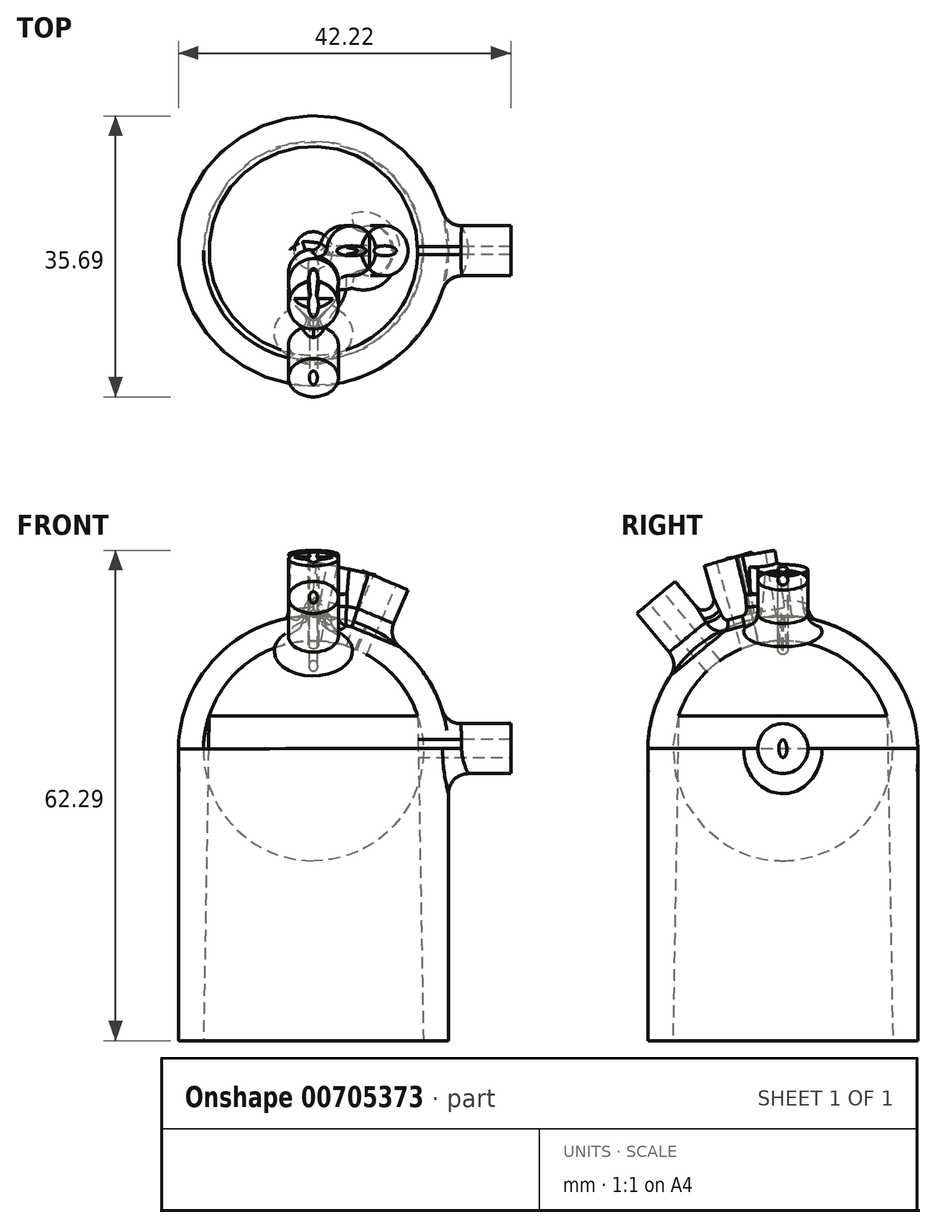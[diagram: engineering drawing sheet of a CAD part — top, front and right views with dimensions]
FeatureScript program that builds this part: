
annotation { "Feature Type Name" : "Feature", "Feature Type Description" : "" }
export const myFeature = defineFeature(function(context is Context, id is Id, definition is map)
    precondition{}
    {
        {
            var Q0;
            Q0=qCreatedBy(makeId("Front.planeOp"),FACE);
            var sketch = newSketch(context, id + "F0", { "sketchPlane" : qUnion([Q0])});
            skPoint(sketch, "E0.orphan", {"position": v(0, 0) * mm});
            skLineSegment(sketch, "E1.right", {"start": v(13.97, 0) * mm, "end": v(13.97, 37.07) * mm});
            skArc(sketch, "E2", {"start": v(13.97, 37.07) * mm, "mid": v(9.8, 46.8) * mm, "end": v(0, 50.8) * mm});
            skArc(sketch, "E3.0", {"start": v(17.14, 37.1) * mm, "mid": v(12.03, 49.05) * mm, "end": v(0, 53.98) * mm});
            skLineSegment(sketch, "E3.1", {"start": v(17.15, 0) * mm, "end": v(17.14, 37.1) * mm});
            skLineSegment(sketch, "E4", {"start": v(0, 53.98) * mm, "end": v(0, 50.8) * mm});
            skLineSegment(sketch, "E5", {"start": v(13.97, 0) * mm, "end": v(17.15, 0) * mm});
            skLineSegment(sketch, "E6", {"start": v(13.97, 0) * mm, "end": v(13.25, 41.26) * mm});
            skSolve(sketch);
        }
        {
            var Q0;
            Q0 = qSketchRegion(id + "F0", true);
            var Q1;
            Q1=sQuery(id+"F0.wireOp",EDGE,"E4");
            revolve(context, id + "F1", {"surfaceOperationType" : NewSurfaceOperationType.NEW, "entities" : qUnion([Q0]), "axis" : qUnion([Q1]), "revolveType" : RevolveType.FULL});
        }
        {
            var Q0;
            Q0=qCreatedBy(makeId("Front.planeOp"),FACE);
            var sketch = newSketch(context, id + "F2", { "sketchPlane" : qUnion([Q0])});
            skPoint(sketch, "E7", {"position": v(0, 37.1) * mm});
            skLineSegment(sketch, "E8", {"start": v(0, 37.1) * mm, "end": v(25.4, 37.1) * mm, "construction": true});
            skLineSegment(sketch, "E9", {"start": v(0, 37.1) * mm, "end": v(9.92, 60.47) * mm, "construction": true});
            skLineSegment(sketch, "E10", {"start": v(0, 37.1) * mm, "end": v(5.28, 61.94) * mm, "construction": true});
            skArc(sketch, "E11.0", {"start": v(6.6, 52.65) * mm, "mid": v(3.37, 53.64) * mm, "end": v(0, 53.98) * mm, "construction": true});
            skPoint(sketch, "E12.orphan", {"position": v(17.14, 37.1) * mm});
            skPoint(sketch, "E13", {"position": v(6.6, 52.65) * mm});
            skPoint(sketch, "E14", {"position": v(3.51, 53.61) * mm});
            skSolve(sketch);
        }
        {
            var Q0;
            Q0=sQuery(id+"F2.wireOp",VERTEX,"E13");
            var Q1;
            Q1=sQuery(id+"F2.wireOp",EDGE,"E9");
            cPlane(context, id + "F3", {"entities" : qUnion([Q0, Q1]), "cplaneType" : CPlaneType.LINE_POINT, "offset" : 25.4 * mm, "width" : 152.4 * mm, "height" : 152.4 * mm});
        }
        {
            var Q0;
            Q0=sQuery(id+"F2.wireOp",VERTEX,"E12.orphan");
            var Q1;
            Q1=sQuery(id+"F2.wireOp",EDGE,"E8");
            cPlane(context, id + "F4", {"entities" : qUnion([Q0, Q1]), "cplaneType" : CPlaneType.LINE_POINT, "offset" : 25.4 * mm, "width" : 152.4 * mm, "height" : 152.4 * mm});
        }
        {
            var Q0;
            Q0=sQuery(id+"F2.wireOp",VERTEX,"E14");
            var Q1;
            Q1=sQuery(id+"F2.wireOp",EDGE,"E10");
            cPlane(context, id + "F5", {"entities" : qUnion([Q0, Q1]), "cplaneType" : CPlaneType.LINE_POINT, "offset" : 25.4 * mm, "width" : 152.4 * mm, "height" : 152.4 * mm});
        }
        {
            var Q0;
            Q0=qCreatedBy(id+"F4.planeOp",FACE);
            var sketch = newSketch(context, id + "F6", { "sketchPlane" : qUnion([Q0])});
            skPoint(sketch, "E15.0", {"position": v(0, 37.1) * mm});
            skCircle(sketch, "E16", {"center": v(0, 37.1) * mm, "radius": 3.18 * mm});
            skSolve(sketch);
        }
        {
            var Q0;
            Q0=makeQuery(id+"F6.imprint","IMPRINT",FACE,{"disambiguationData":[TD([[makeQuery(id+"F6.imprint","IMPRINT",EDGE,{"derivedFrom":sQuery(id+"F6.wireOp",EDGE,"E16")}),1.0]])]});
            extrude(context, id + "F7", {"entities" : qUnion([Q0]), "operationType" : NewBodyOperationType.ADD, "endBound" : BoundingType.SYMMETRIC, "oppositeDirection" : true, "depth" : 3.17 * mm, "offsetDistance" : 25.4 * mm});
        }
        {
            var Q0;
            Q0=makeQuery(id+"F7.opExtrude","CAP_FACE",FACE,{"disambiguationData":[OSD([sQuery(id+"F6.wireOp",EDGE,"E16")])],"isStart":true});
            extrude(context, id + "F8", {"entities" : qUnion([Q0]), "operationType" : NewBodyOperationType.ADD, "depth" : 6.35 * mm, "offsetDistance" : 25.4 * mm});
        }
        {
            var Q0;
            Q0=makeQuery(id+"F8.opExtrude","CAP_FACE",FACE,{"disambiguationData":[OSD([sQuery(id+"F6.wireOp",EDGE,"E16")])],"isStart":false});
            var sketch = newSketch(context, id + "F9", { "sketchPlane" : qUnion([Q0])});
            skEllipse(sketch, "E17", {"center": v(0, 37.1) * mm, "majorRadius": 1.14 * mm, "minorRadius": 0.5 * mm, "majorAxis": v(0, -1)});
            skSolve(sketch);
        }
        {
            var Q0;
            Q0=makeQuery(id+"F9.imprint","IMPRINT",FACE,{"disambiguationData":[TD([[makeQuery(id+"F9.imprint","IMPRINT",EDGE,{"derivedFrom":sQuery(id+"F9.wireOp",EDGE,"E17")}),1.0]])]});
            var Q1;
            Q1=makeQuery(id+"F1.opRevolve","SWEPT_FACE",FACE,{"disambiguationData":[OSD([sQuery(id+"F0.wireOp",EDGE,"E6")])]});
            extrude(context, id + "F10", {"entities" : qUnion([Q0]), "operationType" : NewBodyOperationType.REMOVE, "endBound" : BoundingType.UP_TO_SURFACE, "oppositeDirection" : true, "depth" : 25.4 * mm, "endBoundEntityFace" : qUnion([Q1]), "offsetDistance" : 25.4 * mm});
        }
        {
            var Q0;
            Q0=qCreatedBy(id+"F3.planeOp",FACE);
            var sketch = newSketch(context, id + "F11", { "sketchPlane" : qUnion([Q0])});
            skCircle(sketch, "E18", {"center": v(-14.5, 0) * mm, "radius": 3.18 * mm});
            skSolve(sketch);
        }
        {
            var Q0;
            Q0=makeQuery(id+"F11.imprint","IMPRINT",FACE,{"disambiguationData":[TD([[makeQuery(id+"F11.imprint","IMPRINT",EDGE,{"derivedFrom":sQuery(id+"F11.wireOp",EDGE,"E18")}),1.0]])]});
            extrude(context, id + "F12", {"entities" : qUnion([Q0]), "operationType" : NewBodyOperationType.ADD, "oppositeDirection" : true, "depth" : 3.17 * mm, "offsetDistance" : 25.4 * mm});
        }
        {
            var Q0;
            Q0=makeQuery(id+"F12.opExtrude","CAP_FACE",FACE,{"disambiguationData":[OSD([sQuery(id+"F11.wireOp",EDGE,"E18")])],"isStart":true});
            extrude(context, id + "F13", {"entities" : qUnion([Q0]), "operationType" : NewBodyOperationType.ADD, "depth" : 6.35 * mm, "offsetDistance" : 25.4 * mm});
        }
        {
            var Q0;
            Q0=makeQuery(id+"F13.opExtrude","CAP_FACE",FACE,{"disambiguationData":[OSD([sQuery(id+"F11.wireOp",EDGE,"E18")])],"isStart":false});
            var sketch = newSketch(context, id + "F14", { "sketchPlane" : qUnion([Q0])});
            skEllipse(sketch, "E19", {"center": v(-14.5, 0) * mm, "majorRadius": 1.59 * mm, "minorRadius": 0.64 * mm, "majorAxis": v(1, 0)});
            skSolve(sketch);
        }
        {
            var Q0;
            Q0=qCreatedBy(id+"F5.planeOp",FACE);
            var sketch = newSketch(context, id + "F15", { "sketchPlane" : qUnion([Q0])});
            skCircle(sketch, "E20", {"center": v(-7.71, 0) * mm, "radius": 3.18 * mm});
            skSolve(sketch);
        }
        {
            var Q0;
            Q0=makeQuery(id+"F15.imprint","IMPRINT",FACE,{"disambiguationData":[TD([[makeQuery(id+"F15.imprint","IMPRINT",EDGE,{"derivedFrom":sQuery(id+"F15.wireOp",EDGE,"E20")}),1.0]])]});
            extrude(context, id + "F16", {"entities" : qUnion([Q0]), "operationType" : NewBodyOperationType.ADD, "oppositeDirection" : true, "depth" : 3.17 * mm, "offsetDistance" : 25.4 * mm});
        }
        {
            var Q0;
            Q0=makeQuery(id+"F15.imprint","IMPRINT",FACE,{"disambiguationData":[TD([[makeQuery(id+"F15.imprint","IMPRINT",EDGE,{"derivedFrom":sQuery(id+"F15.wireOp",EDGE,"E20")}),1.0]])]});
            extrude(context, id + "F17", {"entities" : qUnion([Q0]), "operationType" : NewBodyOperationType.ADD, "depth" : 6.35 * mm, "offsetDistance" : 25.4 * mm});
        }
        {
            var Q0;
            Q0=makeQuery(id+"F14.imprint","IMPRINT",FACE,{"disambiguationData":[TD([[makeQuery(id+"F14.imprint","IMPRINT",EDGE,{"derivedFrom":sQuery(id+"F14.wireOp",EDGE,"E19")}),1.0]])]});
            var Q1;
            Q1=makeQuery(id+"F1.opRevolve","SWEPT_FACE",FACE,{"disambiguationData":[OSD([sQuery(id+"F0.wireOp",EDGE,"E2")])]});
            extrude(context, id + "F18", {"entities" : qUnion([Q0]), "operationType" : NewBodyOperationType.REMOVE, "endBound" : BoundingType.SYMMETRIC, "oppositeDirection" : true, "depth" : 25.4 * mm, "endBoundEntityFace" : qUnion([Q1]), "offsetDistance" : 25.4 * mm});
        }
        {
            var Q0;
            Q0=makeQuery(id+"F17.opExtrude","CAP_FACE",FACE,{"disambiguationData":[OSD([sQuery(id+"F15.wireOp",EDGE,"E20")])],"isStart":false});
            var sketch = newSketch(context, id + "F19", { "sketchPlane" : qUnion([Q0])});
            skEllipse(sketch, "E21", {"center": v(-7.71, 0) * mm, "majorRadius": 1.9 * mm, "minorRadius": 0.64 * mm, "majorAxis": v(1, 0)});
            skSolve(sketch);
        }
        {
            var Q0;
            Q0=makeQuery(id+"F19.imprint","IMPRINT",FACE,{"disambiguationData":[TD([[makeQuery(id+"F19.imprint","IMPRINT",EDGE,{"derivedFrom":sQuery(id+"F19.wireOp",EDGE,"E21")}),1.0]])]});
            extrude(context, id + "F20", {"entities" : qUnion([Q0]), "operationType" : NewBodyOperationType.REMOVE, "endBound" : BoundingType.SYMMETRIC, "oppositeDirection" : true, "depth" : 25.4 * mm, "offsetDistance" : 25.4 * mm});
        }
        {
            var Q0;
            Q0=qCreatedBy(makeId("Right.planeOp"),FACE);
            var sketch = newSketch(context, id + "F21", { "sketchPlane" : qUnion([Q0])});
            skPoint(sketch, "E22.0", {"position": v(0, 37.1) * mm});
            skLineSegment(sketch, "E23", {"start": v(0, 37.1) * mm, "end": v(-7, 61.5) * mm, "construction": true});
            skLineSegment(sketch, "E24", {"start": v(0, 37.1) * mm, "end": v(-16.33, 56.55) * mm, "construction": true});
            skLineSegment(sketch, "E25", {"start": v(0, 37.1) * mm, "end": v(-4.2, 62.14) * mm, "construction": true});
            skArc(sketch, "E26", {"start": v(-2.83, 54) * mm, "mid": v(-7.18, 52.66) * mm, "end": v(-11.02, 50.23) * mm, "construction": true});
            skLineSegment(sketch, "E27", {"start": v(0, 37.1) * mm, "end": v(-25.4, 37.1) * mm, "construction": true});
            skPoint(sketch, "E28", {"position": v(-4.73, 53.57) * mm});
            skPoint(sketch, "E29", {"position": v(-11.02, 50.23) * mm});
            skPoint(sketch, "E30", {"position": v(-2.83, 54) * mm});
            skSolve(sketch);
        }
        {
            var Q0;
            {var subQ0=makeQuery(id+"F1.opRevolve","SWEPT_FACE",FACE,{"disambiguationData":[OSD([sQuery(id+"F0.wireOp",EDGE,"E3.0")])]});var subQ1=sQuery(id+"F11.wireOp",EDGE,"E18");var subQ2=makeQuery(id+"F12.opExtrude","SWEPT_FACE",FACE,{"disambiguationData":[OSD([subQ1])]});Q0=makeQuery(id+"F16.boolean.opBoolean","SPLIT",EDGE,{"disambiguationData":[TD([makeQuery(id+"F16.opExtrude","SWEPT_FACE",FACE,{"disambiguationData":[OSD([sQuery(id+"F15.wireOp",EDGE,"E20")])]})])],"derivedFrom":makeQuery(id+"F12.boolean.opBoolean","INTERSECT",EDGE,{"derivedFrom":[subQ0,subQ2]})});}
            var Q1;
            Q1=makeQuery(id+"F16.boolean.opBoolean","INTERSECT",EDGE,{"derivedFrom":[makeQuery(id+"F12.boolean.opBoolean","SPLIT",FACE,{"disambiguationData":[TD([makeQuery(id+"F1.opRevolve","SWEPT_FACE",FACE,{"disambiguationData":[OSD([sQuery(id+"F0.wireOp",EDGE,"E3.1")])]})])],"derivedFrom":makeQuery(id+"F1.opRevolve","SWEPT_FACE",FACE,{"disambiguationData":[OSD([sQuery(id+"F0.wireOp",EDGE,"E3.0")])]})}),makeQuery(id+"F16.opExtrude","SWEPT_FACE",FACE,{"disambiguationData":[OSD([sQuery(id+"F15.wireOp",EDGE,"E20")])]})]});
            var Q2;
            {var subQ0=sQuery(id+"F15.wireOp",EDGE,"E20");var subQ5=makeQuery(id+"F1.opRevolve","SWEPT_FACE",FACE,{"disambiguationData":[OSD([sQuery(id+"F0.wireOp",EDGE,"E3.1")])]});Q2=makeQuery(id+"FIkTwmscGw7EkC1_1.1.F16.boolean.opBoolean","INTERSECT",EDGE,{"derivedFrom":[makeQuery(id+"FIkTwmscGw7EkC1_1.1.F12.boolean.opBoolean","SPLIT",FACE,{"disambiguationData":[TD([subQ5])],"derivedFrom":makeQuery(id+"F16.boolean.opBoolean","SPLIT",FACE,{"disambiguationData":[TD([subQ5])],"derivedFrom":makeQuery(id+"F12.boolean.opBoolean","SPLIT",FACE,{"disambiguationData":[TD([subQ5])],"derivedFrom":makeQuery(id+"F1.opRevolve","SWEPT_FACE",FACE,{"disambiguationData":[OSD([sQuery(id+"F0.wireOp",EDGE,"E3.0")])]})})})}),makeQuery(id+"FIkTwmscGw7EkC1_1.1.F16.opExtrude","SWEPT_FACE",FACE,{"disambiguationData":[OSD([subQ0])]})]});}
            var Q3;
            {var subQ0=sQuery(id+"F11.wireOp",EDGE,"E18");var subQ4=makeQuery(id+"F1.opRevolve","SWEPT_FACE",FACE,{"disambiguationData":[OSD([sQuery(id+"F0.wireOp",EDGE,"E3.1")])]});Q3=makeQuery(id+"FIkTwmscGw7EkC1_1.1.F12.boolean.opBoolean","INTERSECT",EDGE,{"derivedFrom":[makeQuery(id+"F16.boolean.opBoolean","SPLIT",FACE,{"disambiguationData":[TD([subQ4])],"derivedFrom":makeQuery(id+"F12.boolean.opBoolean","SPLIT",FACE,{"disambiguationData":[TD([subQ4])],"derivedFrom":makeQuery(id+"F1.opRevolve","SWEPT_FACE",FACE,{"disambiguationData":[OSD([sQuery(id+"F0.wireOp",EDGE,"E3.0")])]})})}),makeQuery(id+"FIkTwmscGw7EkC1_1.1.F12.opExtrude","SWEPT_FACE",FACE,{"disambiguationData":[OSD([subQ0])]})]});}
            var Q4;
            Q4=makeQuery(id+"F7.boolean.opBoolean","INTERSECT",EDGE,{"derivedFrom":[makeQuery(id+"F1.opRevolve","SWEPT_FACE",FACE,{"disambiguationData":[OSD([sQuery(id+"F0.wireOp",EDGE,"E3.0")])]}),makeQuery(id+"F7.opExtrude","SWEPT_FACE",FACE,{"disambiguationData":[OSD([sQuery(id+"F6.wireOp",EDGE,"E16")])]})]});
            var Q5;
            Q5=makeQuery(id+"F7.boolean.opBoolean","INTERSECT",EDGE,{"derivedFrom":[makeQuery(id+"F1.opRevolve","SWEPT_FACE",FACE,{"disambiguationData":[OSD([sQuery(id+"F0.wireOp",EDGE,"E3.1")])]}),makeQuery(id+"F7.opExtrude","SWEPT_FACE",FACE,{"disambiguationData":[OSD([sQuery(id+"F6.wireOp",EDGE,"E16")])]})]});
            var Q6;
            {var subQ0=sQuery(id+"F6.wireOp",EDGE,"E16");var subQ4=makeQuery(id+"F1.opRevolve","SWEPT_FACE",FACE,{"disambiguationData":[OSD([sQuery(id+"F0.wireOp",EDGE,"E3.1")])]});Q6=makeQuery(id+"FIkTwmscGw7EkC1_1.1.F7.boolean.opBoolean","INTERSECT",EDGE,{"derivedFrom":[makeQuery(id+"F16.boolean.opBoolean","SPLIT",FACE,{"disambiguationData":[TD([subQ4])],"derivedFrom":makeQuery(id+"F12.boolean.opBoolean","SPLIT",FACE,{"disambiguationData":[TD([subQ4])],"derivedFrom":makeQuery(id+"F1.opRevolve","SWEPT_FACE",FACE,{"disambiguationData":[OSD([sQuery(id+"F0.wireOp",EDGE,"E3.0")])]})})}),makeQuery(id+"FIkTwmscGw7EkC1_1.1.F7.opExtrude","SWEPT_FACE",FACE,{"disambiguationData":[OSD([subQ0])]})]});}
            var Q7;
            Q7=makeQuery(id+"FIkTwmscGw7EkC1_1.1.F7.boolean.opBoolean","INTERSECT",EDGE,{"derivedFrom":[makeQuery(id+"F1.opRevolve","SWEPT_FACE",FACE,{"disambiguationData":[OSD([sQuery(id+"F0.wireOp",EDGE,"E3.1")])]}),makeQuery(id+"FIkTwmscGw7EkC1_1.1.F7.opExtrude","SWEPT_FACE",FACE,{"disambiguationData":[OSD([sQuery(id+"F6.wireOp",EDGE,"E16")])]})]});
            fillet(context, id + "F22", {"entities" : qUnion([Q0, Q1, Q2, Q3, Q4, Q5, Q6, Q7]), "radius" : 2.54 * mm, "tangentPropagation" : true, "allowEdgeOverflow" : false});
        }
        {
            var Q0;
            Q0=sQuery(id+"F21.wireOp",VERTEX,"E29");
            var Q1;
            Q1=sQuery(id+"F21.wireOp",EDGE,"E24");
            cPlane(context, id + "F23", {"entities" : qUnion([Q0, Q1]), "cplaneType" : CPlaneType.LINE_POINT, "offset" : 25.4 * mm, "width" : 152.4 * mm, "height" : 152.4 * mm});
        }
        {
            var Q0;
            Q0=sQuery(id+"F21.wireOp",VERTEX,"E28");
            var Q1;
            Q1=sQuery(id+"F21.wireOp",EDGE,"E23");
            cPlane(context, id + "F24", {"entities" : qUnion([Q0, Q1]), "cplaneType" : CPlaneType.LINE_POINT, "offset" : 25.4 * mm, "width" : 152.4 * mm, "height" : 152.4 * mm});
        }
        {
            var Q0;
            Q0=sQuery(id+"F21.wireOp",VERTEX,"E30");
            var Q1;
            Q1=sQuery(id+"F21.wireOp",EDGE,"E25");
            cPlane(context, id + "F25", {"entities" : qUnion([Q0, Q1]), "cplaneType" : CPlaneType.LINE_POINT, "offset" : 25.4 * mm, "width" : 152.4 * mm, "height" : 152.4 * mm});
        }
        {
            var Q0;
            Q0=qCreatedBy(id+"F23.planeOp",FACE);
            var sketch = newSketch(context, id + "F26", { "sketchPlane" : qUnion([Q0])});
            skPoint(sketch, "E31.0", {"position": v(0, 23.84) * mm});
            skCircle(sketch, "E32", {"center": v(0, 23.84) * mm, "radius": 3.18 * mm});
            skSolve(sketch);
        }
        {
            var Q0;
            Q0=makeQuery(id+"F26.imprint","IMPRINT",FACE,{"disambiguationData":[TD([[makeQuery(id+"F26.imprint","IMPRINT",EDGE,{"derivedFrom":sQuery(id+"F26.wireOp",EDGE,"E32")}),1.0]])]});
            extrude(context, id + "F27", {"entities" : qUnion([Q0]), "operationType" : NewBodyOperationType.ADD, "endBound" : BoundingType.SYMMETRIC, "depth" : 3.17 * mm, "offsetDistance" : 25.4 * mm});
        }
        {
            var Q0;
            Q0=makeQuery(id+"F27.opExtrude","CAP_FACE",FACE,{"disambiguationData":[OSD([sQuery(id+"F26.wireOp",EDGE,"E32")])],"isStart":false});
            extrude(context, id + "F28", {"entities" : qUnion([Q0]), "operationType" : NewBodyOperationType.ADD, "depth" : 6.35 * mm, "offsetDistance" : 25.4 * mm});
        }
        {
            var Q0;
            Q0=qCreatedBy(id+"F24.planeOp",FACE);
            var sketch = newSketch(context, id + "F29", { "sketchPlane" : qUnion([Q0])});
            skPoint(sketch, "E33.0", {"position": v(0, 10.22) * mm});
            skCircle(sketch, "E34", {"center": v(0, 10.22) * mm, "radius": 3.18 * mm});
            skSolve(sketch);
        }
        {
            var Q0;
            Q0=makeQuery(id+"F29.imprint","IMPRINT",FACE,{"disambiguationData":[TD([[makeQuery(id+"F29.imprint","IMPRINT",EDGE,{"derivedFrom":sQuery(id+"F29.wireOp",EDGE,"E34")}),1.0]])]});
            extrude(context, id + "F30", {"entities" : qUnion([Q0]), "operationType" : NewBodyOperationType.ADD, "endBound" : BoundingType.SYMMETRIC, "depth" : 3.17 * mm, "offsetDistance" : 25.4 * mm});
        }
        {
            var Q0;
            Q0=makeQuery(id+"F30.opExtrude","CAP_FACE",FACE,{"disambiguationData":[OSD([sQuery(id+"F29.wireOp",EDGE,"E34")])],"isStart":false});
            extrude(context, id + "F31", {"entities" : qUnion([Q0]), "operationType" : NewBodyOperationType.ADD, "depth" : 6.35 * mm, "offsetDistance" : 25.4 * mm});
        }
        {
            var Q0;
            Q0=qCreatedBy(id+"F25.planeOp",FACE);
            var sketch = newSketch(context, id + "F32", { "sketchPlane" : qUnion([Q0])});
            skPoint(sketch, "E35.0", {"position": v(0, 6.12) * mm});
            skCircle(sketch, "E36", {"center": v(0, 6.12) * mm, "radius": 3.18 * mm});
            skSolve(sketch);
        }
        {
            var Q0;
            Q0 = qSketchRegion(id + "F32", true);
            extrude(context, id + "F33", {"entities" : qUnion([Q0]), "operationType" : NewBodyOperationType.ADD, "endBound" : BoundingType.SYMMETRIC, "depth" : 3.17 * mm, "offsetDistance" : 25.4 * mm});
        }
        {
            var Q0;
            Q0 = qSketchRegion(id + "F32", true);
            extrude(context, id + "F34", {"entities" : qUnion([Q0]), "operationType" : NewBodyOperationType.ADD, "depth" : 7.87 * mm, "offsetDistance" : 25.4 * mm});
        }
        {
            var Q0;
            Q0=makeQuery(id+"F28.opExtrude","CAP_FACE",FACE,{"disambiguationData":[OSD([sQuery(id+"F26.wireOp",EDGE,"E32")])],"isStart":false});
            var sketch = newSketch(context, id + "F35", { "sketchPlane" : qUnion([Q0])});
            skEllipse(sketch, "E37", {"center": v(0, 23.84) * mm, "majorRadius": 1.14 * mm, "minorRadius": 0.5 * mm, "majorAxis": v(0, -1)});
            skSolve(sketch);
        }
        {
            var Q0;
            Q0 = qSketchRegion(id + "F35", true);
            extrude(context, id + "F36", {"entities" : qUnion([Q0]), "operationType" : NewBodyOperationType.REMOVE, "oppositeDirection" : true, "depth" : 25.4 * mm, "offsetDistance" : 25.4 * mm});
        }
        {
            var Q0;
            Q0=makeQuery(id+"F31.opExtrude","CAP_FACE",FACE,{"disambiguationData":[OSD([sQuery(id+"F29.wireOp",EDGE,"E34")])],"isStart":false});
            var sketch = newSketch(context, id + "F37", { "sketchPlane" : qUnion([Q0])});
            skEllipse(sketch, "E38", {"center": v(0, 10.22) * mm, "majorRadius": 1.59 * mm, "minorRadius": 0.64 * mm, "majorAxis": v(0, -1)});
            skSolve(sketch);
        }
        {
            var Q0;
            Q0 = qSketchRegion(id + "F37", true);
            extrude(context, id + "F38", {"entities" : qUnion([Q0]), "operationType" : NewBodyOperationType.REMOVE, "endBound" : BoundingType.SYMMETRIC, "oppositeDirection" : true, "depth" : 25.4 * mm, "offsetDistance" : 25.4 * mm});
        }
        {
            var Q0;
            {var subQ0=sQuery(id+"F29.wireOp",EDGE,"E34");var subQ1=sQuery(id+"F32.wireOp",EDGE,"E36");Q0=makeQuery(id+"F34.boolean.opBoolean","SPLIT",FACE,{"disambiguationData":[TD([makeQuery(id+"F30.opExtrude","SWEPT_FACE",FACE,{"disambiguationData":[OSD([subQ0])]})])],"derivedFrom":makeQuery(id+"F34.opExtrude","CAP_FACE",FACE,{"disambiguationData":[OSD([subQ1])],"isStart":false})});}
            var sketch = newSketch(context, id + "F39", { "sketchPlane" : qUnion([Q0])});
            skEllipse(sketch, "E39", {"center": v(0, 6.12) * mm, "majorRadius": 1.9 * mm, "minorRadius": 0.64 * mm, "majorAxis": v(0, 1)});
            skSolve(sketch);
        }
        {
            var Q0;
            Q0 = qSketchRegion(id + "F39", true);
            extrude(context, id + "F40", {"entities" : qUnion([Q0]), "operationType" : NewBodyOperationType.REMOVE, "endBound" : BoundingType.SYMMETRIC, "oppositeDirection" : true, "depth" : 25.4 * mm, "offsetDistance" : 25.4 * mm});
        }
        {
            var Q0;
            {var subQ4=makeQuery(id+"F1.opRevolve","SWEPT_FACE",FACE,{"disambiguationData":[OSD([sQuery(id+"F0.wireOp",EDGE,"E3.1")])]});Q0=makeQuery(id+"F27.boolean.opBoolean","INTERSECT",EDGE,{"derivedFrom":[makeQuery(id+"FIkTwmscGw7EkC1_1.1.F12.boolean.opBoolean","SPLIT",FACE,{"disambiguationData":[TD([subQ4])],"derivedFrom":makeQuery(id+"F16.boolean.opBoolean","SPLIT",FACE,{"disambiguationData":[TD([subQ4])],"derivedFrom":makeQuery(id+"F12.boolean.opBoolean","SPLIT",FACE,{"disambiguationData":[TD([subQ4])],"derivedFrom":makeQuery(id+"F1.opRevolve","SWEPT_FACE",FACE,{"disambiguationData":[OSD([sQuery(id+"F0.wireOp",EDGE,"E3.0")])]})})})}),makeQuery(id+"F27.opExtrude","SWEPT_FACE",FACE,{"disambiguationData":[OSD([sQuery(id+"F26.wireOp",EDGE,"E32")])]})]});}
            var Q1;
            {var subQ4=makeQuery(id+"F1.opRevolve","SWEPT_FACE",FACE,{"disambiguationData":[OSD([sQuery(id+"F0.wireOp",EDGE,"E3.1")])]});Q1=makeQuery(id+"F0e8zPmASTsI8iK_1.1.F27.boolean.opBoolean","INTERSECT",EDGE,{"derivedFrom":[makeQuery(id+"FIkTwmscGw7EkC1_1.1.F12.boolean.opBoolean","SPLIT",FACE,{"disambiguationData":[TD([subQ4])],"derivedFrom":makeQuery(id+"F16.boolean.opBoolean","SPLIT",FACE,{"disambiguationData":[TD([subQ4])],"derivedFrom":makeQuery(id+"F12.boolean.opBoolean","SPLIT",FACE,{"disambiguationData":[TD([subQ4])],"derivedFrom":makeQuery(id+"F1.opRevolve","SWEPT_FACE",FACE,{"disambiguationData":[OSD([sQuery(id+"F0.wireOp",EDGE,"E3.0")])]})})})}),makeQuery(id+"F0e8zPmASTsI8iK_1.1.F27.opExtrude","SWEPT_FACE",FACE,{"disambiguationData":[OSD([sQuery(id+"F26.wireOp",EDGE,"E32")])]})]});}
            fillet(context, id + "F41", {"entities" : qUnion([Q0, Q1]), "radius" : 2.54 * mm, "tangentPropagation" : true, "allowEdgeOverflow" : false});
        }
        {
            var Q0;
            {var subQ0=sQuery(id+"F29.wireOp",EDGE,"E34");Q0=makeQuery(id+"F0e8zPmASTsI8iK_1.1.F34.boolean.opBoolean","INTERSECT",EDGE,{"disambiguationData":[OD(0.0)],"derivedFrom":[makeQuery(id+"F0e8zPmASTsI8iK_1.1.F31.boolean.opBoolean","MERGE",FACE,{"derivedFrom":[makeQuery(id+"F0e8zPmASTsI8iK_1.1.F30.opExtrude","SWEPT_FACE",FACE,{"disambiguationData":[OSD([subQ0])]}),makeQuery(id+"F0e8zPmASTsI8iK_1.1.F31.opExtrude","SWEPT_FACE",FACE,{"disambiguationData":[OSD([subQ0])]})]}),makeQuery(id+"F0e8zPmASTsI8iK_1.1.F34.opExtrude","SWEPT_FACE",FACE,{"disambiguationData":[OSD([sQuery(id+"F32.wireOp",EDGE,"E36")])]})]});}
            var Q1;
            {var subQ0=sQuery(id+"F29.wireOp",EDGE,"E34");Q1=makeQuery(id+"F34.boolean.opBoolean","INTERSECT",EDGE,{"disambiguationData":[OD(0.0)],"derivedFrom":[makeQuery(id+"F31.boolean.opBoolean","MERGE",FACE,{"derivedFrom":[makeQuery(id+"F30.opExtrude","SWEPT_FACE",FACE,{"disambiguationData":[OSD([subQ0])]}),makeQuery(id+"F31.opExtrude","SWEPT_FACE",FACE,{"disambiguationData":[OSD([subQ0])]})]}),makeQuery(id+"F34.opExtrude","SWEPT_FACE",FACE,{"disambiguationData":[OSD([sQuery(id+"F32.wireOp",EDGE,"E36")])]})]});}
            var Q2;
            {var subQ0=sQuery(id+"F29.wireOp",EDGE,"E34");Q2=makeQuery(id+"F0e8zPmASTsI8iK_1.1.F34.boolean.opBoolean","INTERSECT",EDGE,{"disambiguationData":[OD(1.0)],"derivedFrom":[makeQuery(id+"F0e8zPmASTsI8iK_1.1.F31.boolean.opBoolean","MERGE",FACE,{"derivedFrom":[makeQuery(id+"F0e8zPmASTsI8iK_1.1.F30.opExtrude","SWEPT_FACE",FACE,{"disambiguationData":[OSD([subQ0])]}),makeQuery(id+"F0e8zPmASTsI8iK_1.1.F31.opExtrude","SWEPT_FACE",FACE,{"disambiguationData":[OSD([subQ0])]})]}),makeQuery(id+"F0e8zPmASTsI8iK_1.1.F34.opExtrude","SWEPT_FACE",FACE,{"disambiguationData":[OSD([sQuery(id+"F32.wireOp",EDGE,"E36")])]})]});}
            var Q3;
            {var subQ0=sQuery(id+"F29.wireOp",EDGE,"E34");Q3=makeQuery(id+"F34.boolean.opBoolean","INTERSECT",EDGE,{"disambiguationData":[OD(1.0)],"derivedFrom":[makeQuery(id+"F31.boolean.opBoolean","MERGE",FACE,{"derivedFrom":[makeQuery(id+"F30.opExtrude","SWEPT_FACE",FACE,{"disambiguationData":[OSD([subQ0])]}),makeQuery(id+"F31.opExtrude","SWEPT_FACE",FACE,{"disambiguationData":[OSD([subQ0])]})]}),makeQuery(id+"F34.opExtrude","SWEPT_FACE",FACE,{"disambiguationData":[OSD([sQuery(id+"F32.wireOp",EDGE,"E36")])]})]});}
            fillet(context, id + "F42", {"entities" : qUnion([Q0, Q1, Q2, Q3]), "radius" : 1.27 * mm, "tangentPropagation" : true, "allowEdgeOverflow" : false});
        }
        {
            var Q0;
            {var subQ4=makeQuery(id+"F1.opRevolve","SWEPT_FACE",FACE,{"disambiguationData":[OSD([sQuery(id+"F0.wireOp",EDGE,"E3.1")])]});Q0=makeQuery(id+"F0e8zPmASTsI8iK_1.1.F30.boolean.opBoolean","INTERSECT",EDGE,{"derivedFrom":[makeQuery(id+"FIkTwmscGw7EkC1_1.1.F12.boolean.opBoolean","SPLIT",FACE,{"disambiguationData":[TD([subQ4])],"derivedFrom":makeQuery(id+"F16.boolean.opBoolean","SPLIT",FACE,{"disambiguationData":[TD([subQ4])],"derivedFrom":makeQuery(id+"F12.boolean.opBoolean","SPLIT",FACE,{"disambiguationData":[TD([subQ4])],"derivedFrom":makeQuery(id+"F1.opRevolve","SWEPT_FACE",FACE,{"disambiguationData":[OSD([sQuery(id+"F0.wireOp",EDGE,"E3.0")])]})})})}),makeQuery(id+"F0e8zPmASTsI8iK_1.1.F30.opExtrude","SWEPT_FACE",FACE,{"disambiguationData":[OSD([sQuery(id+"F29.wireOp",EDGE,"E34")])]})]});}
            var Q1;
            {var subQ4=makeQuery(id+"F1.opRevolve","SWEPT_FACE",FACE,{"disambiguationData":[OSD([sQuery(id+"F0.wireOp",EDGE,"E3.1")])]});Q1=makeQuery(id+"F30.boolean.opBoolean","INTERSECT",EDGE,{"derivedFrom":[makeQuery(id+"FIkTwmscGw7EkC1_1.1.F12.boolean.opBoolean","SPLIT",FACE,{"disambiguationData":[TD([subQ4])],"derivedFrom":makeQuery(id+"F16.boolean.opBoolean","SPLIT",FACE,{"disambiguationData":[TD([subQ4])],"derivedFrom":makeQuery(id+"F12.boolean.opBoolean","SPLIT",FACE,{"disambiguationData":[TD([subQ4])],"derivedFrom":makeQuery(id+"F1.opRevolve","SWEPT_FACE",FACE,{"disambiguationData":[OSD([sQuery(id+"F0.wireOp",EDGE,"E3.0")])]})})})}),makeQuery(id+"F30.opExtrude","SWEPT_FACE",FACE,{"disambiguationData":[OSD([sQuery(id+"F29.wireOp",EDGE,"E34")])]})]});}
            fillet(context, id + "F43", {"entities" : qUnion([Q0, Q1]), "radius" : 1.27 * mm, "tangentPropagation" : true, "allowEdgeOverflow" : false});
        }
    });
